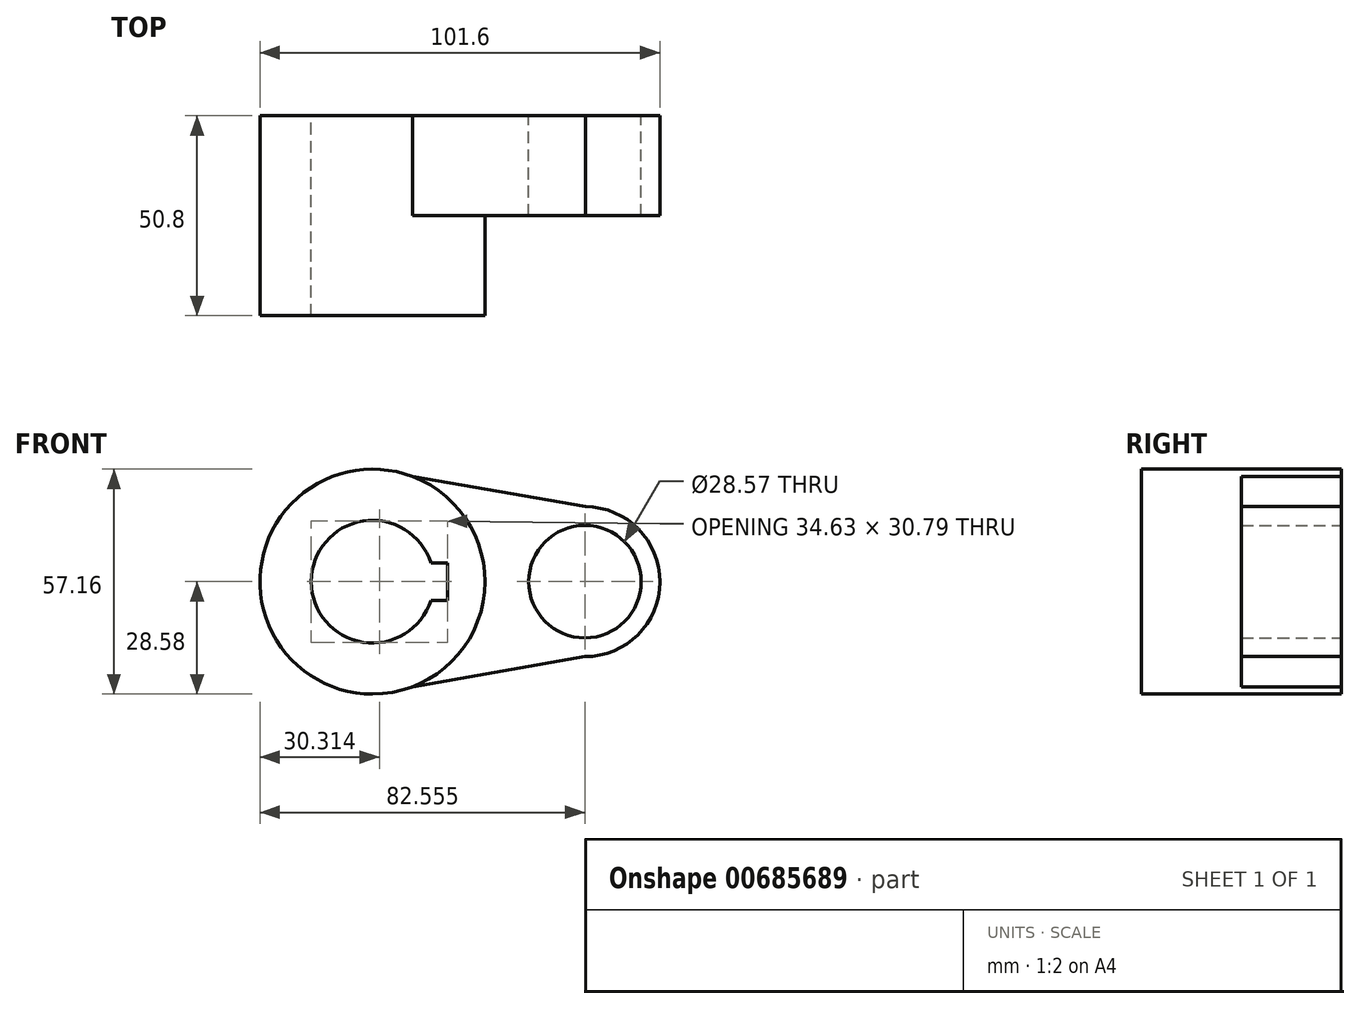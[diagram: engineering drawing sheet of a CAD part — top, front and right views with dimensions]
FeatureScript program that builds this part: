
annotation { "Feature Type Name" : "Feature", "Feature Type Description" : "" }
export const myFeature = defineFeature(function(context is Context, id is Id, definition is map)
    precondition{}
    {
        {
            var Q0;
            Q0=qCreatedBy(makeId("Front.planeOp"),FACE);
            var sketch = newSketch(context, id + "F0", { "sketchPlane" : qUnion([Q0])});
            skCircle(sketch, "E0", {"center": v(0, 0) * mm, "radius": 28.58 * mm});
            skCircle(sketch, "E1", {"center": v(53.98, 0) * mm, "radius": 19.05 * mm});
            skLineSegment(sketch, "E2", {"start": v(10.14, 26.72) * mm, "end": v(54.13, 19.05) * mm});
            skLineSegment(sketch, "E3", {"start": v(10.14, -26.72) * mm, "end": v(53.98, -19.05) * mm});
            skCircle(sketch, "E4", {"center": v(0, 0) * mm, "radius": 15.58 * mm});
            skCircle(sketch, "E5", {"center": v(53.98, 0) * mm, "radius": 14.29 * mm});
            skLineSegment(sketch, "E6.bottom", {"start": v(-19.05, -4.76) * mm, "end": v(19.05, -4.76) * mm});
            skLineSegment(sketch, "E6.top", {"start": v(-19.05, 4.76) * mm, "end": v(19.05, 4.76) * mm});
            skLineSegment(sketch, "E6.left", {"start": v(-19.05, -4.76) * mm, "end": v(-19.05, 4.76) * mm});
            skLineSegment(sketch, "E6.right", {"start": v(19.05, -4.76) * mm, "end": v(19.05, 4.76) * mm});
            skSolve(sketch);
        }
        {
            var Q0;
            {var subQ7=sQuery(id+"F0.wireOp",EDGE,"E6.left");Q0=makeQuery(id+"F0.imprint","IMPRINT",FACE,{"disambiguationData":[TD([[makeQuery(id+"F0.imprint","IMPRINT",EDGE,{"derivedFrom":subQ7}),1.0]])]});}
            var Q1;
            {var subQ0=sQuery(id+"F0.wireOp",EDGE,"E2");Q1=makeQuery(id+"F0.imprint","IMPRINT",FACE,{"disambiguationData":[TD([[makeQuery(id+"F0.imprint","IMPRINT",EDGE,{"derivedFrom":subQ0}),-1.0]])]});}
            var Q2;
            Q2=makeQuery(id+"F0.imprint","IMPRINT",FACE,{"disambiguationData":[TD([[makeQuery(id+"F0.imprint","IMPRINT",EDGE,{"derivedFrom":sQuery(id+"F0.wireOp",EDGE,"E5")}),-1.0]])]});
            var Q3;
            {var subQ5=sQuery(id+"F0.wireOp",EDGE,"E6.left");Q3=makeQuery(id+"F0.imprint","IMPRINT",FACE,{"disambiguationData":[TD([[makeQuery(id+"F0.imprint","IMPRINT",EDGE,{"derivedFrom":subQ5}),-1.0]])]});}
            extrude(context, id + "F1", {"entities" : qUnion([Q0, Q1, Q2, Q3]), "depth" : 25.4 * mm, "offsetDistance" : 25.4 * mm});
        }
        {
            var Q0;
            {var subQ7=sQuery(id+"F0.wireOp",EDGE,"E6.left");Q0=makeQuery(id+"F0.imprint","IMPRINT",FACE,{"disambiguationData":[TD([[makeQuery(id+"F0.imprint","IMPRINT",EDGE,{"derivedFrom":subQ7}),1.0]])]});}
            var Q1;
            {var subQ5=sQuery(id+"F0.wireOp",EDGE,"E6.left");Q1=makeQuery(id+"F0.imprint","IMPRINT",FACE,{"disambiguationData":[TD([[makeQuery(id+"F0.imprint","IMPRINT",EDGE,{"derivedFrom":subQ5}),-1.0]])]});}
            extrude(context, id + "F2", {"entities" : qUnion([Q0, Q1]), "operationType" : NewBodyOperationType.ADD, "depth" : 50.8 * mm, "offsetDistance" : 25.4 * mm});
        }
    });
